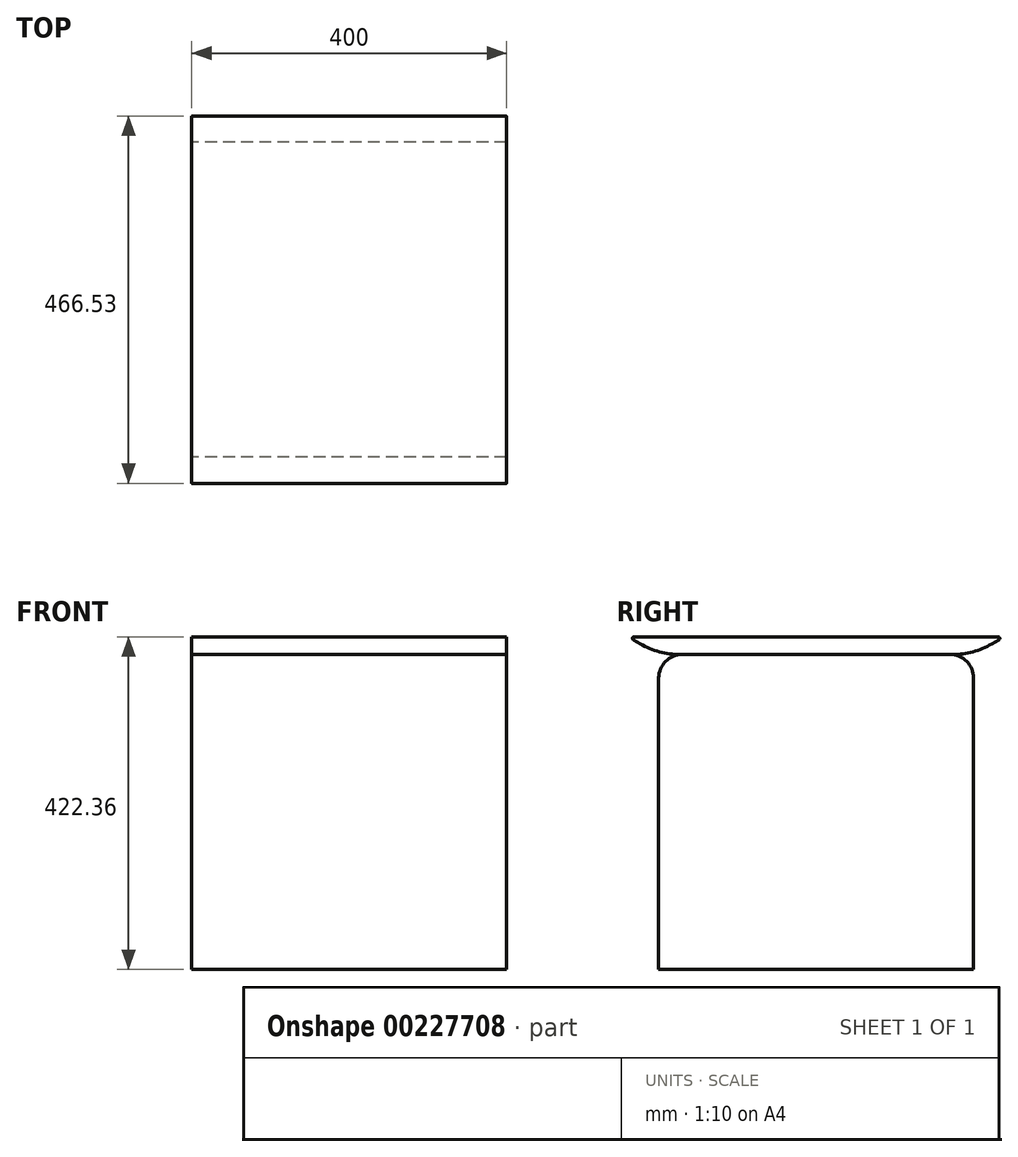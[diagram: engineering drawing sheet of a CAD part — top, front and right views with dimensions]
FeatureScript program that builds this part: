
annotation { "Feature Type Name" : "Feature", "Feature Type Description" : "" }
export const myFeature = defineFeature(function(context is Context, id is Id, definition is map)
    precondition{}
    {
        {
            var Q0;
            Q0=qCreatedBy(makeId("Right.planeOp"),FACE);
            var sketch = newSketch(context, id + "F0", { "sketchPlane" : qUnion([Q0])});
            skLineSegment(sketch, "E0", {"start": v(-182.8, -218.93) * mm, "end": v(-182.8, 181.07) * mm});
            skLineSegment(sketch, "E1", {"start": v(-182.8, 181.07) * mm, "end": v(-221.54, 203.43) * mm});
            skLineSegment(sketch, "E2", {"start": v(217.2, 181.07) * mm, "end": v(217.2, -218.93) * mm});
            skLineSegment(sketch, "E3", {"start": v(217.2, -218.93) * mm, "end": v(-182.8, -218.93) * mm});
            skLineSegment(sketch, "E4", {"start": v(17.2, -218.93) * mm, "end": v(17.2, 181.07) * mm, "construction": true});
            skLineSegment(sketch, "E5.MirrorCS", {"start": v(217.2, 181.07) * mm, "end": v(255.92, 203.43) * mm});
            skLineSegment(sketch, "E6", {"start": v(-221.54, 203.43) * mm, "end": v(255.92, 203.43) * mm});
            skLineSegment(sketch, "E7", {"start": v(-182.8, 181.07) * mm, "end": v(217.2, 181.07) * mm});
            skSolve(sketch);
        }
        {
            var Q0;
            Q0=makeQuery(id+"F0.imprint","IMPRINT",FACE,{"disambiguationData":[TD([[makeQuery(id+"F0.imprint","IMPRINT",EDGE,{"derivedFrom":sQuery(id+"F0.wireOp",EDGE,"E0")}),-1.0]])]});
            extrude(context, id + "F1", {"entities" : qUnion([Q0]), "depth" : 400 * mm, "symmetric" : true});
        }
        {
            var Q0;
            Q0=makeQuery(id+"F0.imprint","IMPRINT",FACE,{"disambiguationData":[TD([[makeQuery(id+"F0.imprint","IMPRINT",EDGE,{"derivedFrom":sQuery(id+"F0.wireOp",EDGE,"E1")}),-1.0]])]});
            extrude(context, id + "F2", {"entities" : qUnion([Q0]), "depth" : 400 * mm, "symmetric" : true});
        }
        {
            var Q0;
            Q0=makeQuery(id+"F1.opExtrude","SWEPT_EDGE",EDGE,{"disambiguationData":[OSD([sQuery(id+"F0.wireOp",EDGE,"E0"),sQuery(id+"F0.wireOp",EDGE,"E1"),sQuery(id+"F0.wireOp",EDGE,"E7")])]});
            var Q1;
            Q1=makeQuery(id+"F1.opExtrude","SWEPT_EDGE",EDGE,{"disambiguationData":[OSD([sQuery(id+"F0.wireOp",EDGE,"E2"),sQuery(id+"F0.wireOp",EDGE,"E5.MirrorCS"),sQuery(id+"F0.wireOp",EDGE,"E7")])]});
            fillet(context, id + "F3", {"entities" : qUnion([Q0, Q1]), "radius" : 30 * mm, "tangentPropagation" : true, "allowEdgeOverflow" : false});
        }
        {
            var Q0;
            Q0=makeQuery(id+"F2.opExtrude","SWEPT_EDGE",EDGE,{"disambiguationData":[OSD([sQuery(id+"F0.wireOp",EDGE,"E2"),sQuery(id+"F0.wireOp",EDGE,"E5.MirrorCS"),sQuery(id+"F0.wireOp",EDGE,"E7")])]});
            var Q1;
            Q1=makeQuery(id+"F2.opExtrude","SWEPT_EDGE",EDGE,{"disambiguationData":[OSD([sQuery(id+"F0.wireOp",EDGE,"E0"),sQuery(id+"F0.wireOp",EDGE,"E1"),sQuery(id+"F0.wireOp",EDGE,"E7")])]});
            fillet(context, id + "F4", {"entities" : qUnion([Q0, Q1]), "radius" : 100 * mm, "tangentPropagation" : true, "allowEdgeOverflow" : false});
        }
        {
            var Q0;
            Q0=makeQuery(id+"F2.opExtrude","SWEPT_EDGE",EDGE,{"disambiguationData":[OSD([sQuery(id+"F0.wireOp",EDGE,"E5.MirrorCS"),sQuery(id+"F0.wireOp",EDGE,"E6")])]});
            var Q1;
            Q1=makeQuery(id+"F2.opExtrude","SWEPT_EDGE",EDGE,{"disambiguationData":[OSD([sQuery(id+"F0.wireOp",EDGE,"E1"),sQuery(id+"F0.wireOp",EDGE,"E6")])]});
            fillet(context, id + "F5", {"entities" : qUnion([Q0, Q1]), "radius" : 2 * mm, "tangentPropagation" : true, "allowEdgeOverflow" : false});
        }
    });
